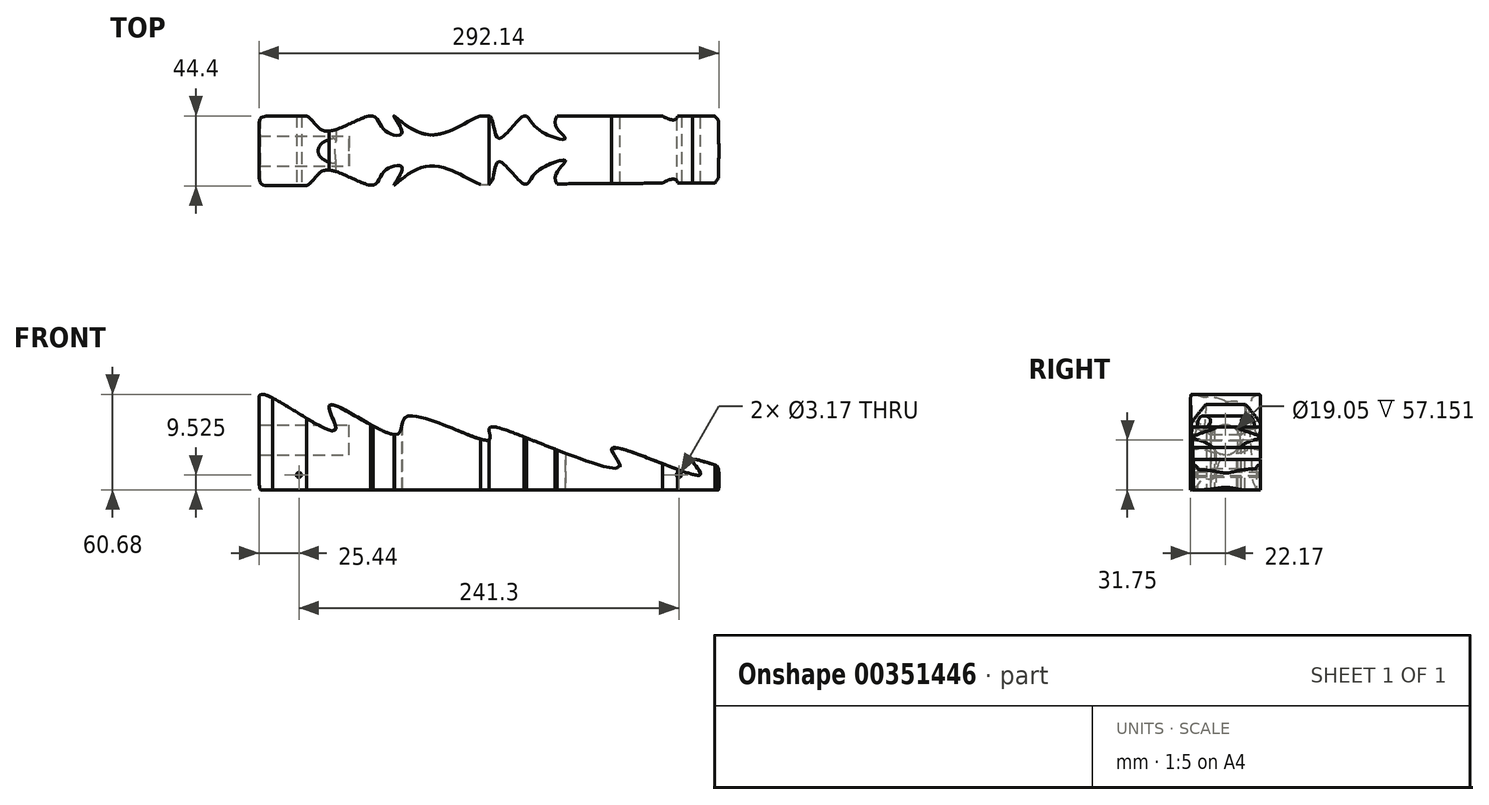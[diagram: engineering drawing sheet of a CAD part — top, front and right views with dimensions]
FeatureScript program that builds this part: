
annotation { "Feature Type Name" : "Feature", "Feature Type Description" : "" }
export const myFeature = defineFeature(function(context is Context, id is Id, definition is map)
    precondition{}
    {
        {
            var Q0;
            Q0=qCreatedBy(makeId("Front.planeOp"),FACE);
            var sketch = newSketch(context, id + "F0", { "sketchPlane" : qUnion([Q0])});
            skLineSegment(sketch, "E0.bottom", {"start": v(-146, 28.96) * mm, "end": v(146.1, 28.96) * mm, "construction": true});
            skLineSegment(sketch, "E0.top", {"start": v(-146.05, -34.54) * mm, "end": v(146.1, -34.54) * mm, "construction": true});
            skLineSegment(sketch, "E0.left", {"start": v(-146, 28.96) * mm, "end": v(-146, -34.54) * mm, "construction": true});
            skLineSegment(sketch, "E0.right", {"start": v(146.1, 28.96) * mm, "end": v(146.1, -34.54) * mm, "construction": true});
            skFitSpline(sketch, "E1", {"points": [v(-144.22, -32.92) * mm, v(-146, -21.08) * mm, v(-146, 26.74) * mm, v(-145.64, 28.33) * mm, v(-140.54, 28.13) * mm, v(-97.4, 6.14) * mm, v(-101.25, 22.15) * mm, v(-58.29, 3.44) * mm, v(-52.54, 14.74) * mm, v(0, 0) * mm, v(0.02, 6.73) * mm, v(16.24, 4.27) * mm, v(83.29, -16.79) * mm, v(78.28, -5.18) * mm, v(134.2, -22.18) * mm, v(129.26, -12.93) * mm, v(138.37, -14.32) * mm, v(144.96, -16.72) * mm, v(146.1, -22.42) * mm, v(145.34, -33.69) * mm, v(142.58, -34.54) * mm, v(122.29, -34.54) * mm, v(105.92, -34.54) * mm, v(84.4, -34.54) * mm, v(65.4, -34.54) * mm, v(52.9, -34.54) * mm, v(27.18, -34.54) * mm, v(11.2, -34.54) * mm, v(-14.99, -34.54) * mm, v(-49.5, -34.54) * mm, v(-69.86, -34.54) * mm, v(-91.85, -34.54) * mm, v(-107.6, -34.54) * mm, v(-122.3, -34.54) * mm, v(-137.35, -34.54) * mm, v(-144.22, -32.92) * mm]});
            skLineSegment(sketch, "E2", {"start": v(-146, 28.96) * mm, "end": v(146.1, -15.5) * mm, "construction": true});
            skSolve(sketch);
        }
        {
            var Q0;
            Q0=qCreatedBy(makeId("Top.planeOp"),FACE);
            var sketch = newSketch(context, id + "F1", { "sketchPlane" : qUnion([Q0])});
            skLineSegment(sketch, "E3.bottom", {"start": v(-146.05, 22.22) * mm, "end": v(146.05, 22.22) * mm, "construction": true});
            skLineSegment(sketch, "E3.top", {"start": v(-146.05, -22.23) * mm, "end": v(146.05, -22.22) * mm, "construction": true});
            skLineSegment(sketch, "E3.left", {"start": v(-146.05, 22.22) * mm, "end": v(-146.05, -22.23) * mm, "construction": true});
            skLineSegment(sketch, "E3.right", {"start": v(146.05, 24.2) * mm, "end": v(146.05, -22.22) * mm, "construction": true});
            skLineSegment(sketch, "E4", {"start": v(-146.05, 0) * mm, "end": v(146.05, 0.99) * mm, "construction": true});
            skFitSpline(sketch, "E5", {"points": [v(-146.05, 0) * mm, v(-146.08, 12.32) * mm, v(-144.83, 20.85) * mm, v(-137.04, 22.26) * mm, v(-115.65, 22.13) * mm, v(-103.46, 12.5) * mm, v(-73.8, 22.22) * mm, v(-66.37, 13.35) * mm, v(-55.32, 11.22) * mm, v(-60.25, 22.22) * mm, v(-37.35, 10.2) * mm, v(0, 22.22) * mm, v(6.08, 7.94) * mm, v(22.2, 22.22) * mm, v(30.03, 14.78) * mm, v(48.58, 7.65) * mm, v(41.9, 18.43) * mm, v(80.4, 35.6) * mm, v(109.76, 22.38) * mm, v(119.7, 21.8) * mm, v(114.76, 51.44) * mm, v(145.1, 20.03) * mm, v(145.77, 18.35) * mm, v(146.05, 0.99) * mm], "startDerivative": vector(0, 335.54) * mm, "endDerivative": vector(0.01, -277.49) * mm});
            skFitSpline(sketch, "E6.MirrorCS", {"points": [v(-146.05, 0) * mm, v(-146, -12.32) * mm, v(-144.69, -20.84) * mm, v(-136.89, -22.2) * mm, v(-115.5, -21.93) * mm, v(-103.37, -12.21) * mm, v(-73.64, -21.74) * mm, v(-66.29, -12.82) * mm, v(-55.25, -10.6) * mm, v(-60.1, -21.65) * mm, v(-37.28, -9.46) * mm, v(0.15, -21.24) * mm, v(6.13, -6.9) * mm, v(22.34, -21.09) * mm, v(30.13, -13.6) * mm, v(48.62, -6.34) * mm, v(42.01, -17.17) * mm, v(80.64, -34.08) * mm, v(109.9, -20.65) * mm, v(119.83, -20) * mm, v(115.1, -49.68) * mm, v(145.23, -18.06) * mm, v(145.9, -16.38) * mm, v(146.05, 0.99) * mm], "startDerivative": vector(2.26, -335.53) * mm, "endDerivative": vector(-1.86, 277.48) * mm});
            skLineSegment(sketch, "E7.MirrorCS", {"start": v(-145.9, -22.22) * mm, "end": v(146.2, -20.25) * mm});
            skSolve(sketch);
        }
        {
            var Q0;
            Q0=qCreatedBy(makeId("Right.planeOp"),FACE);
            var sketch = newSketch(context, id + "F2", { "sketchPlane" : qUnion([Q0])});
            skCircle(sketch, "E8", {"center": v(0, 0) * mm, "radius": 9.53 * mm});
            skSolve(sketch);
        }
        {
            var Q0;
            Q0=qCreatedBy(makeId("Front.planeOp"),FACE);
            var sketch = newSketch(context, id + "F3", { "sketchPlane" : qUnion([Q0])});
            skCircle(sketch, "E9", {"center": v(-120.65, -22.22) * mm, "radius": 1.59 * mm});
            skCircle(sketch, "E10", {"center": v(120.65, -22.23) * mm, "radius": 1.59 * mm});
            skSolve(sketch);
        }
        {
            var Q0;
            Q0=qSketchRegion(id+"F0",true);
            extrude(context, id + "F4", {"entities" : qUnion([Q0]), "depth" : 44.45 * mm, "symmetric" : true});
        }
        {
            var Q0;
            Q0=makeQuery(id+"F1.imprint","IMPRINT",FACE,{"disambiguationData":[TD([[makeQuery(id+"F1.imprint","IMPRINT",EDGE,{"derivedFrom":sQuery(id+"F1.wireOp",EDGE,"E5")}),-1.0]])]});
            var Q1;
            Q1=sQuery(id+"F1.wireOp",EDGE,"E6.MirrorCS");
            var Q2;
            Q2=sQuery(id+"F1.wireOp",EDGE,"E5");
            extrude(context, id + "F5", {"entities" : qUnion([Q0]), "operationType" : NewBodyOperationType.INTERSECT, "surfaceEntities" : qUnion([Q1, Q2]), "oppositeDirection" : true, "depth" : 63.5 * mm, "symmetric" : true});
        }
        {
            var Q0;
            Q0=qSketchRegion(id+"F2",true);
            extrude(context, id + "F6", {"entities" : qUnion([Q0]), "operationType" : NewBodyOperationType.REMOVE, "oppositeDirection" : true, "depth" : 152.4 * mm, "hasSecondDirection" : true, "secondDirectionOppositeDirection" : true, "secondDirectionDepth" : 88.9 * mm});
        }
        {
            var Q0;
            Q0=qSketchRegion(id+"F3",true);
            extrude(context, id + "F7", {"entities" : qUnion([Q0]), "operationType" : NewBodyOperationType.REMOVE, "oppositeDirection" : true, "depth" : 50.8 * mm, "symmetric" : true});
        }
    });
